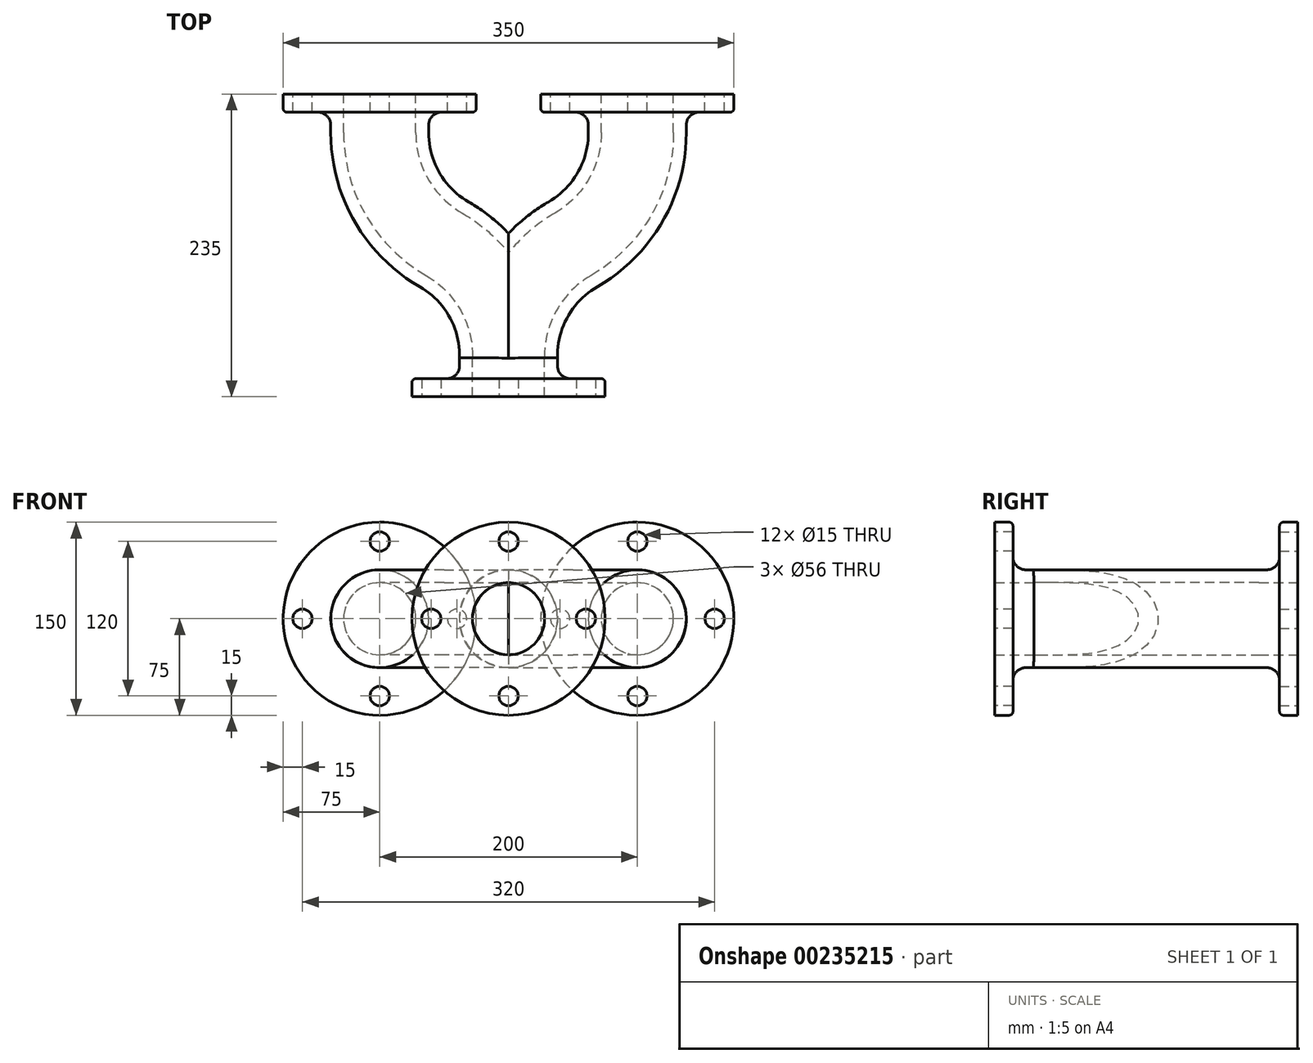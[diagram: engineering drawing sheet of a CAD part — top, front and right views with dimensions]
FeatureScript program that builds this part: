
annotation { "Feature Type Name" : "Feature", "Feature Type Description" : "" }
export const myFeature = defineFeature(function(context is Context, id is Id, definition is map)
    precondition{}
    {
        {
            var Q0;
            Q0=qCreatedBy(makeId("Top.planeOp"),FACE);
            var sketch = newSketch(context, id + "F0", { "sketchPlane" : qUnion([Q0])});
            skLineSegment(sketch, "E0", {"start": v(0, 0) * mm, "end": v(0, 30) * mm});
            skLineSegment(sketch, "E1", {"start": v(-100, 235) * mm, "end": v(-100, 205) * mm});
            skArc(sketch, "E2", {"start": v(-100, 205) * mm, "mid": v(-86.6, 155) * mm, "end": v(-50, 118.4) * mm});
            skArc(sketch, "E3", {"start": v(0, 30) * mm, "mid": v(-12.95, 81.02) * mm, "end": v(-50, 118.4) * mm});
            skSolve(sketch);
        }
        {
            var Q0;
            Q0=qCreatedBy(makeId("Front.planeOp"),FACE);
            var sketch = newSketch(context, id + "F1", { "sketchPlane" : qUnion([Q0])});
            skCircle(sketch, "E4", {"center": v(0, 0) * mm, "radius": 28 * mm});
            skCircle(sketch, "E5.0", {"center": v(0, 0) * mm, "radius": 38 * mm});
            skSolve(sketch);
        }
        {
            var Q0;
            Q0=makeQuery(id+"F1.imprint","IMPRINT",FACE,{"disambiguationData":[TD([[makeQuery(id+"F1.imprint","IMPRINT",EDGE,{"derivedFrom":sQuery(id+"F1.wireOp",EDGE,"E4")}),-1.0]])]});
            var Q1;
            Q1 = qConstructionFilter(qBodyType(qCreatedBy(id + "F0" ,EDGE), BodyType.WIRE), ConstructionObject.NO);
            sweep(context, id + "F2", {"profiles" : qUnion([Q0]), "path" : qUnion([Q1])});
        }
        {
            var Q0;
            Q0=qCreatedBy(makeId("Front.planeOp"),FACE);
            var sketch = newSketch(context, id + "F3", { "sketchPlane" : qUnion([Q0])});
            skLineSegment(sketch, "E6", {"start": v(0, -38) * mm, "end": v(0, 38) * mm});
            skArc(sketch, "E7.0", {"start": v(0, -43) * mm, "mid": v(43, 0) * mm, "end": v(0, 43) * mm});
            skLineSegment(sketch, "E8", {"start": v(0, 38) * mm, "end": v(0, 43) * mm});
            skLineSegment(sketch, "E9", {"start": v(0, -38) * mm, "end": v(0, -43) * mm});
            skSolve(sketch);
        }
        {
            var Q0;
            Q0 = qSketchRegion(id + "F3", true);
            extrude(context, id + "F4", {"entities" : qUnion([Q0]), "operationType" : NewBodyOperationType.REMOVE, "endBound" : BoundingType.THROUGH_ALL, "oppositeDirection" : true, "depth" : 25 * mm});
        }
        {
            var Q0;
            Q0=makeQuery(id+"F2.opSweep","CAP_FACE",FACE,{"disambiguationData":[OSD([sQuery(id+"F0.wireOp",VERTEX,"E1.start"),sQuery(id+"F1.wireOp",EDGE,"E4"),sQuery(id+"F1.wireOp",EDGE,"E5.0")])],"isStart":false});
            var sketch = newSketch(context, id + "F5", { "sketchPlane" : qUnion([Q0])});
            skCircle(sketch, "E10.0", {"center": v(100, 0) * mm, "radius": 33 * mm});
            skCircle(sketch, "E11", {"center": v(100, 0) * mm, "radius": 75 * mm});
            skCircle(sketch, "E12", {"center": v(100, 0) * mm, "radius": 60 * mm, "construction": true});
            skCircle(sketch, "E13", {"center": v(100, 60) * mm, "radius": 7.5 * mm});
            skCircle(sketch, "E14.1.0", {"center": v(40, 0) * mm, "radius": 7.5 * mm});
            skCircle(sketch, "E14.2.0", {"center": v(100, -60) * mm, "radius": 7.5 * mm});
            skCircle(sketch, "E15.1.3.0", {"center": v(160, 0) * mm, "radius": 7.5 * mm});
            skSolve(sketch);
        }
        {
            var Q0;
            Q0 = qSketchRegion(id + "F5", true);
            var Q1;
            Q1=makeQuery(id+"F5.imprint","IMPRINT",FACE,{"disambiguationData":[TD([[makeQuery(id+"F5.imprint","IMPRINT",EDGE,{"derivedFrom":sQuery(id+"F5.wireOp",EDGE,"E10.0")}),1.0]])]});
            extrude(context, id + "F6", {"entities" : qUnion([Q0, Q1]), "operationType" : NewBodyOperationType.ADD, "oppositeDirection" : true, "depth" : 14 * mm});
        }
        {
            var Q0;
            Q0=makeQuery(id+"F6.boolean.opBoolean","INTERSECT",EDGE,{"derivedFrom":[makeQuery(id+"F2.opSweep","SWEPT_FACE",FACE,{"disambiguationData":[OSD([sQuery(id+"F0.wireOp",EDGE,"E1"),sQuery(id+"F1.wireOp",EDGE,"E5.0")])]}),makeQuery(id+"F6.opExtrude","CAP_FACE",FACE,{"disambiguationData":[OSD([sQuery(id+"F0.wireOp",VERTEX,"E1.start"),sQuery(id+"F1.wireOp",EDGE,"E4"),sQuery(id+"F5.wireOp",EDGE,"E11"),sQuery(id+"F5.wireOp",EDGE,"E13"),sQuery(id+"F5.wireOp",EDGE,"E14.1.0"),sQuery(id+"F5.wireOp",EDGE,"E14.2.0"),sQuery(id+"F5.wireOp",EDGE,"E15.1.3.0")])],"isStart":false})]});
            fillet(context, id + "F7", {"entities" : qUnion([Q0]), "radius" : 10 * mm, "tangentPropagation" : true, "allowEdgeOverflow" : false});
        }
        {
            var Q0;
            Q0=makeQuery(id+"F6.opExtrude","CAP_EDGE",EDGE,{"disambiguationData":[OSD([sQuery(id+"F5.wireOp",EDGE,"E11")])],"isStart":false});
            fillet(context, id + "F8", {"entities" : qUnion([Q0]), "radius" : 3 * mm, "tangentPropagation" : true, "allowEdgeOverflow" : false});
        }
        {
            var Q0;
            Q0=makeQuery(id+"F2.opSweep","SWEPT_BODY",BODY,{"disambiguationData":[OSD([sQuery(id+"F0.wireOp",EDGE,"E1"),sQuery(id+"F1.wireOp",EDGE,"E4"),sQuery(id+"F1.wireOp",EDGE,"E5.0")])]});
            var Q1;
            Q1=qCreatedBy(makeId("Right.planeOp"),FACE);
            mirror(context, id + "F9", {"operationType" : NewBodyOperationType.ADD, "entities" : qUnion([Q0]), "mirrorPlane" : qUnion([Q1])});
        }
        {
            var Q0;
            Q0=qCreatedBy(makeId("Front.planeOp"),FACE);
            var sketch = newSketch(context, id + "F10", { "sketchPlane" : qUnion([Q0])});
            skCircle(sketch, "E16.0", {"center": v(0, 0) * mm, "radius": 33 * mm});
            skCircle(sketch, "E17", {"center": v(0, 0) * mm, "radius": 75 * mm});
            skCircle(sketch, "E18", {"center": v(0, 0) * mm, "radius": 60 * mm, "construction": true});
            skCircle(sketch, "E19", {"center": v(0, 60) * mm, "radius": 7.5 * mm});
            skCircle(sketch, "E20.1.0", {"center": v(-60, 0) * mm, "radius": 7.5 * mm});
            skCircle(sketch, "E20.2.0", {"center": v(0, -60) * mm, "radius": 7.5 * mm});
            skCircle(sketch, "E21.1.3.0", {"center": v(60, 0) * mm, "radius": 7.5 * mm});
            skSolve(sketch);
        }
        {
            var Q0;
            Q0 = qSketchRegion(id + "F10", true);
            var Q1;
            {var subQ0=makeQuery(id+"F2.opSweep","CAP_FACE",FACE,{"disambiguationData":[OSD([sQuery(id+"F0.wireOp",VERTEX,"E0.start"),sQuery(id+"F1.wireOp",EDGE,"E4"),sQuery(id+"F1.wireOp",EDGE,"E5.0")])],"isStart":true});Q1=makeQuery(id+"F9.boolean.opBoolean","MERGE",FACE,{"derivedFrom":[subQ0,makeQuery(id+"F9.opPattern","COPY",FACE,{"derivedFrom":subQ0,"instanceName":"1"})]});}
            extrude(context, id + "F11", {"entities" : qUnion([Q0, Q1]), "operationType" : NewBodyOperationType.ADD, "oppositeDirection" : true, "depth" : 14 * mm});
        }
        {
            var Q0;
            {var subQ0=sQuery(id+"F1.wireOp",EDGE,"E5.0");var subQ1=makeQuery(id+"F2.opSweep","SWEPT_FACE",FACE,{"disambiguationData":[OSD([sQuery(id+"F0.wireOp",EDGE,"E0"),subQ0])]});Q0=makeQuery(id+"F11.boolean.opBoolean","INTERSECT",EDGE,{"derivedFrom":[makeQuery(id+"F9.boolean.opBoolean","MERGE",FACE,{"derivedFrom":[subQ1,makeQuery(id+"F9.opPattern","COPY",FACE,{"derivedFrom":subQ1,"instanceName":"1"})]}),makeQuery(id+"F11.opExtrude","CAP_FACE",FACE,{"disambiguationData":[OSD([sQuery(id+"F0.wireOp",VERTEX,"E0.start"),sQuery(id+"F1.wireOp",EDGE,"E4"),subQ0])],"isStart":false}),makeQuery(id+"F11.opExtrude","CAP_FACE",FACE,{"disambiguationData":[OSD([sQuery(id+"F10.wireOp",EDGE,"E16.0"),sQuery(id+"F10.wireOp",EDGE,"E17"),sQuery(id+"F10.wireOp",EDGE,"E19"),sQuery(id+"F10.wireOp",EDGE,"E20.1.0"),sQuery(id+"F10.wireOp",EDGE,"E20.2.0"),sQuery(id+"F10.wireOp",EDGE,"E21.1.3.0")])],"isStart":false})]});}
            fillet(context, id + "F12", {"entities" : qUnion([Q0]), "radius" : 10 * mm, "tangentPropagation" : true, "allowEdgeOverflow" : false});
        }
        {
            var Q0;
            Q0=makeQuery(id+"F11.opExtrude","CAP_EDGE",EDGE,{"disambiguationData":[OSD([sQuery(id+"F10.wireOp",EDGE,"E17")])],"isStart":false});
            fillet(context, id + "F13", {"entities" : qUnion([Q0]), "radius" : 3 * mm, "tangentPropagation" : true, "allowEdgeOverflow" : false});
        }
    });
